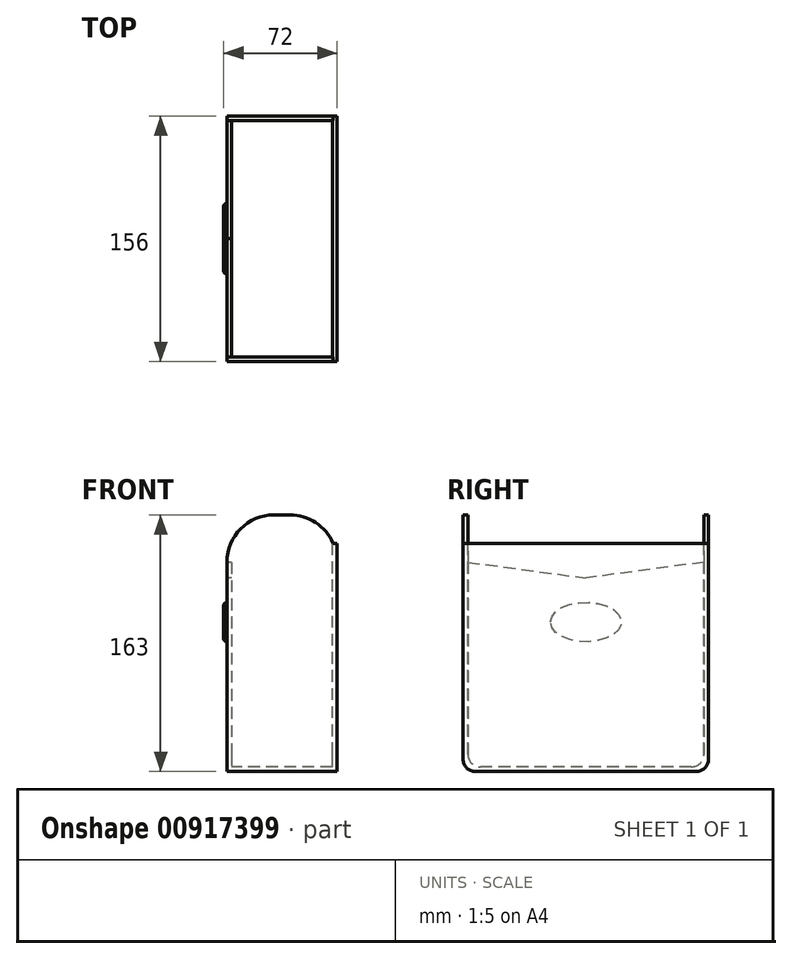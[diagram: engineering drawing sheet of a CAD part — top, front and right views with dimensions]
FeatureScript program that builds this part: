
annotation { "Feature Type Name" : "Feature", "Feature Type Description" : "" }
export const myFeature = defineFeature(function(context is Context, id is Id, definition is map)
    precondition{}
    {
        {
            var Q0;
            Q0=qCreatedBy(makeId("Right.planeOp"),FACE);
            var sketch = newSketch(context, id + "F0", { "sketchPlane" : qUnion([Q0])});
            skLineSegment(sketch, "E0", {"start": v(-78, 163) * mm, "end": v(-78, 8) * mm});
            skLineSegment(sketch, "E1", {"start": v(-70, 0) * mm, "end": v(0, 0) * mm});
            skLineSegment(sketch, "E2", {"start": v(0, 0) * mm, "end": v(0, 3) * mm});
            skLineSegment(sketch, "E3", {"start": v(0, 3) * mm, "end": v(-67, 3) * mm});
            skLineSegment(sketch, "E4", {"start": v(-75, 11) * mm, "end": v(-75, 163) * mm});
            skLineSegment(sketch, "E5", {"start": v(-75, 163) * mm, "end": v(-78, 163) * mm});
            skPoint(sketch, "E6.visualSharp", {"position": v(-75, 3) * mm});
            skArc(sketch, "E6.filletArc", {"start": v(-75, 11) * mm, "mid": v(-72.66, 5.34) * mm, "end": v(-67, 3) * mm});
            skPoint(sketch, "E7.visualSharp", {"position": v(-78, 0) * mm});
            skArc(sketch, "E7.filletArc", {"start": v(-78, 8) * mm, "mid": v(-75.66, 2.34) * mm, "end": v(-70, 0) * mm});
            skArc(sketch, "E8.MirrorCS", {"start": v(78, 8) * mm, "mid": v(75.66, 2.34) * mm, "end": v(70, 0) * mm});
            skArc(sketch, "E9.MirrorCS", {"start": v(75, 11) * mm, "mid": v(72.66, 5.34) * mm, "end": v(67, 3) * mm});
            skLineSegment(sketch, "E10.MirrorCS", {"start": v(70, 0) * mm, "end": v(0, 0) * mm});
            skLineSegment(sketch, "E11.MirrorCS", {"start": v(0, 3) * mm, "end": v(67, 3) * mm});
            skLineSegment(sketch, "E12.MirrorCS", {"start": v(75, 163) * mm, "end": v(78, 163) * mm});
            skLineSegment(sketch, "E13.MirrorCS", {"start": v(75, 11) * mm, "end": v(75, 163) * mm});
            skLineSegment(sketch, "E14.MirrorCS", {"start": v(78, 163) * mm, "end": v(78, 8) * mm});
            skPoint(sketch, "E15.MirrorP", {"position": v(78, 0) * mm});
            skPoint(sketch, "E16.MirrorP", {"position": v(75, 3) * mm});
            skSolve(sketch);
        }
        {
            var Q0;
            Q0 = qSketchRegion(id + "F0", true);
            extrude(context, id + "F1", {"entities" : qUnion([Q0]), "endBound" : BoundingType.SYMMETRIC, "depth" : 70 * mm, "offsetDistance" : 25 * mm});
        }
        {
            var Q0;
            Q0=makeQuery(id+"F1.opExtrude","CAP_EDGE",EDGE,{"disambiguationData":[OSD([sQuery(id+"F0.wireOp",EDGE,"E5")])],"isStart":false});
            var Q1;
            Q1=makeQuery(id+"F1.opExtrude","CAP_EDGE",EDGE,{"disambiguationData":[OSD([sQuery(id+"F0.wireOp",EDGE,"E12.MirrorCS")])],"isStart":false});
            var Q2;
            Q2=makeQuery(id+"F1.opExtrude","CAP_EDGE",EDGE,{"disambiguationData":[OSD([sQuery(id+"F0.wireOp",EDGE,"E12.MirrorCS")])],"isStart":true});
            var Q3;
            Q3=makeQuery(id+"F1.opExtrude","CAP_EDGE",EDGE,{"disambiguationData":[OSD([sQuery(id+"F0.wireOp",EDGE,"E5")])],"isStart":true});
            fillet(context, id + "F2", {"entities" : qUnion([Q0, Q1, Q2, Q3]), "radius" : 30 * mm, "tangentPropagation" : true, "allowEdgeOverflow" : false});
        }
        {
            var Q0;
            Q0=makeQuery(id+"F1.opExtrude","CAP_FACE",FACE,{"disambiguationData":[OSD([sQuery(id+"F0.wireOp",EDGE,"E0"),sQuery(id+"F0.wireOp",EDGE,"E1"),sQuery(id+"F0.wireOp",EDGE,"E3"),sQuery(id+"F0.wireOp",EDGE,"E4"),sQuery(id+"F0.wireOp",EDGE,"E5"),sQuery(id+"F0.wireOp",EDGE,"E6.filletArc"),sQuery(id+"F0.wireOp",EDGE,"E7.filletArc"),sQuery(id+"F0.wireOp",EDGE,"E8.MirrorCS"),sQuery(id+"F0.wireOp",EDGE,"E9.MirrorCS"),sQuery(id+"F0.wireOp",EDGE,"E10.MirrorCS"),sQuery(id+"F0.wireOp",EDGE,"E11.MirrorCS"),sQuery(id+"F0.wireOp",EDGE,"E12.MirrorCS"),sQuery(id+"F0.wireOp",EDGE,"E13.MirrorCS"),sQuery(id+"F0.wireOp",EDGE,"E14.MirrorCS")])],"isStart":true});
            cPlane(context, id + "F3", {"entities" : qUnion([Q0]), "cplaneType" : CPlaneType.OFFSET, "offset" : 0 * mm, "width" : 150 * mm, "height" : 150 * mm});
        }
        {
            var Q0;
            Q0=qCreatedBy(id+"F3.planeOp",FACE);
            var sketch = newSketch(context, id + "F4", { "sketchPlane" : qUnion([Q0])});
            skLineSegment(sketch, "E17", {"start": v(-78, 133) * mm, "end": v(-75, 133) * mm});
            skLineSegment(sketch, "E18", {"start": v(0, 0) * mm, "end": v(-70, 0) * mm});
            skLineSegment(sketch, "E19", {"start": v(-78, 8) * mm, "end": v(-78, 133) * mm});
            skPoint(sketch, "E20.visualSharp", {"position": v(-78, 0) * mm});
            skArc(sketch, "E20.filletArc", {"start": v(-78, 8) * mm, "mid": v(-75.66, 2.34) * mm, "end": v(-70, 0) * mm});
            skLineSegment(sketch, "E21", {"start": v(-75, 133) * mm, "end": v(0, 123) * mm});
            skLineSegment(sketch, "E22.MirrorCS", {"start": v(78, 133) * mm, "end": v(75, 133) * mm});
            skArc(sketch, "E23.MirrorCS", {"start": v(78, 8) * mm, "mid": v(75.66, 2.34) * mm, "end": v(70, 0) * mm});
            skLineSegment(sketch, "E24.MirrorCS", {"start": v(0, 123) * mm, "end": v(0, 0) * mm, "construction": true});
            skPoint(sketch, "E25.MirrorP", {"position": v(78, 0) * mm});
            skLineSegment(sketch, "E26.MirrorCS", {"start": v(78, 8) * mm, "end": v(78, 133) * mm});
            skLineSegment(sketch, "E27.MirrorCS", {"start": v(0, 0) * mm, "end": v(70, 0) * mm});
            skLineSegment(sketch, "E28.MirrorCS", {"start": v(75, 133) * mm, "end": v(0, 123) * mm});
            skSolve(sketch);
        }
        {
            var Q0;
            Q0=makeQuery(id+"F4.imprint","IMPRINT",FACE,{"disambiguationData":[TD([[makeQuery(id+"F4.imprint","IMPRINT",EDGE,{"derivedFrom":sQuery(id+"F4.wireOp",EDGE,"E17")}),-1.0]])]});
            extrude(context, id + "F5", {"entities" : qUnion([Q0]), "operationType" : NewBodyOperationType.ADD, "oppositeDirection" : true, "depth" : 3 * mm, "offsetDistance" : 25 * mm});
        }
        {
            var Q0;
            Q0=makeQuery(id+"F1.opExtrude","CAP_FACE",FACE,{"disambiguationData":[OSD([sQuery(id+"F0.wireOp",EDGE,"E0"),sQuery(id+"F0.wireOp",EDGE,"E1"),sQuery(id+"F0.wireOp",EDGE,"E3"),sQuery(id+"F0.wireOp",EDGE,"E4"),sQuery(id+"F0.wireOp",EDGE,"E5"),sQuery(id+"F0.wireOp",EDGE,"E6.filletArc"),sQuery(id+"F0.wireOp",EDGE,"E7.filletArc"),sQuery(id+"F0.wireOp",EDGE,"E8.MirrorCS"),sQuery(id+"F0.wireOp",EDGE,"E9.MirrorCS"),sQuery(id+"F0.wireOp",EDGE,"E10.MirrorCS"),sQuery(id+"F0.wireOp",EDGE,"E11.MirrorCS"),sQuery(id+"F0.wireOp",EDGE,"E12.MirrorCS"),sQuery(id+"F0.wireOp",EDGE,"E13.MirrorCS"),sQuery(id+"F0.wireOp",EDGE,"E14.MirrorCS")])],"isStart":false});
            cPlane(context, id + "F6", {"entities" : qUnion([Q0]), "cplaneType" : CPlaneType.OFFSET, "offset" : 0 * mm, "width" : 150 * mm, "height" : 150 * mm});
        }
        {
            var Q0;
            Q0=qCreatedBy(id+"F6.planeOp",FACE);
            var sketch = newSketch(context, id + "F7", { "sketchPlane" : qUnion([Q0])});
            skLineSegment(sketch, "E29", {"start": v(-78, 8) * mm, "end": v(-78, 145) * mm});
            skLineSegment(sketch, "E30", {"start": v(-78, 145) * mm, "end": v(0, 145) * mm});
            skLineSegment(sketch, "E31", {"start": v(0, 145) * mm, "end": v(0, 0) * mm, "construction": true});
            skLineSegment(sketch, "E32", {"start": v(0, 0) * mm, "end": v(-70, 0) * mm});
            skPoint(sketch, "E33.visualSharp", {"position": v(-78, 0) * mm});
            skArc(sketch, "E33.filletArc", {"start": v(-78, 8) * mm, "mid": v(-75.66, 2.34) * mm, "end": v(-70, 0) * mm});
            skLineSegment(sketch, "E34.MirrorCS", {"start": v(78, 145) * mm, "end": v(0, 145) * mm});
            skLineSegment(sketch, "E35.MirrorCS", {"start": v(78, 8) * mm, "end": v(78, 145) * mm});
            skArc(sketch, "E36.MirrorCS", {"start": v(78, 8) * mm, "mid": v(75.66, 2.34) * mm, "end": v(70, 0) * mm});
            skLineSegment(sketch, "E37.MirrorCS", {"start": v(0, 0) * mm, "end": v(70, 0) * mm});
            skSolve(sketch);
        }
        {
            var Q0;
            Q0=makeQuery(id+"F7.imprint","IMPRINT",FACE,{"disambiguationData":[TD([[makeQuery(id+"F7.imprint","IMPRINT",EDGE,{"derivedFrom":sQuery(id+"F7.wireOp",EDGE,"E29")}),-1.0]])]});
            extrude(context, id + "F8", {"entities" : qUnion([Q0]), "operationType" : NewBodyOperationType.ADD, "oppositeDirection" : true, "depth" : 3 * mm, "offsetDistance" : 25 * mm});
        }
        {
            var Q0;
            Q0=qCreatedBy(id+"F3.planeOp",FACE);
            var sketch = newSketch(context, id + "F9", { "sketchPlane" : qUnion([Q0])});
            skEllipse(sketch, "E38", {"center": v(0, 95) * mm, "majorRadius": 22.5 * mm, "minorRadius": 12.5 * mm, "majorAxis": v(1, 0)});
            skSolve(sketch);
        }
        {
            var Q0;
            Q0=makeQuery(id+"F9.imprint","IMPRINT",FACE,{"disambiguationData":[TD([[makeQuery(id+"F9.imprint","IMPRINT",EDGE,{"derivedFrom":sQuery(id+"F9.wireOp",EDGE,"E38")}),1.0]])]});
            extrude(context, id + "F10", {"entities" : qUnion([Q0]), "operationType" : NewBodyOperationType.ADD, "depth" : 2 * mm, "offsetDistance" : 25 * mm});
        }
        {
            var Q0;
            Q0=makeQuery(id+"F10.opExtrude","CAP_EDGE",EDGE,{"disambiguationData":[OSD([sQuery(id+"F9.wireOp",EDGE,"E38")])],"isStart":false});
            fillet(context, id + "F11", {"entities" : qUnion([Q0]), "radius" : 2 * mm, "tangentPropagation" : true, "allowEdgeOverflow" : false});
        }
    });
